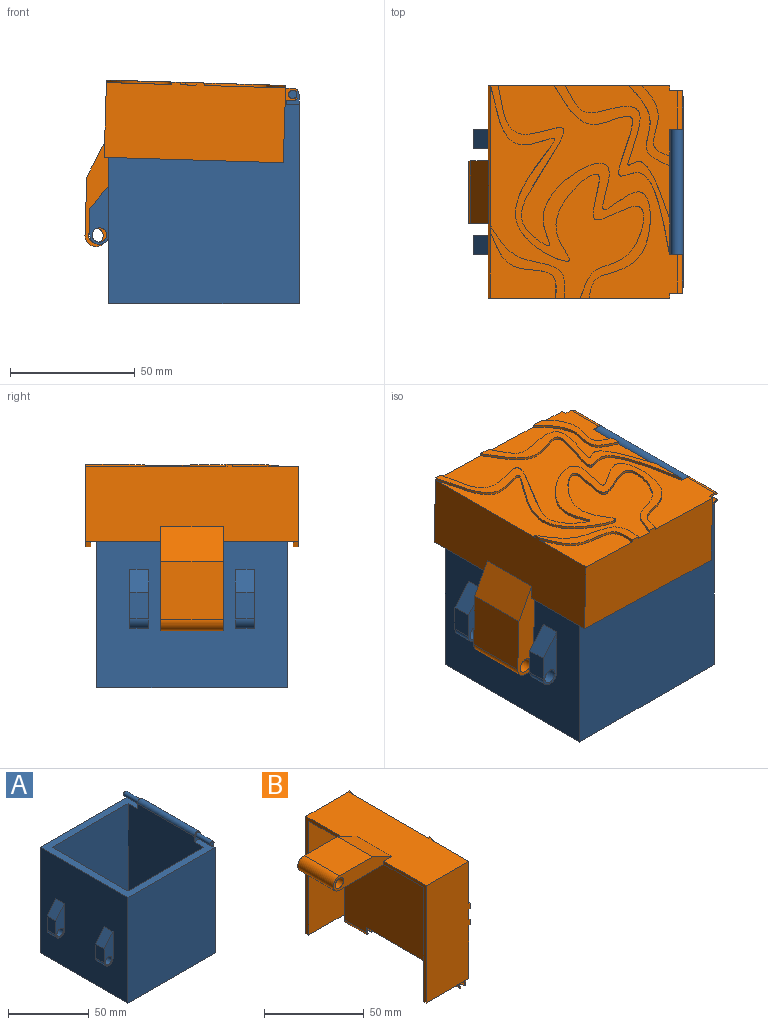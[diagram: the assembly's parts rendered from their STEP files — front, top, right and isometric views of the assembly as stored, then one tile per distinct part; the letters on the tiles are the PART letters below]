
ASSEMBLY  parts=2 mates=1
PART A: 30 faces, bbox 83.9x76.2x86.5 mm
  f0: plane 76.2x76.2mm, normal (0,0,1), area 1174mm2, adj f1,f2,f3,f4,f6,f7,f8,f9
  f1: plane 80x76.2mm, normal (0,-1,0), area 6096mm2, adj f0,f2,f4,f5
  f2: plane 84x76.2mm, normal (1,0,0), area 6296mm2, adj f0,f1,f3,f5,f11,f12,f13
  f3: plane 80x76.2mm, normal (0,1,0), area 6096mm2, adj f0,f2,f4,f5
  f4: plane 80x76.2mm, normal (-1,0,0), area 5796mm2, adj f0,f1,f3,f5,f18,f20,f22,f23
  f5: plane 76.2x76.2mm, normal (0,0,-1), area 5806.4mm2, adj f1,f2,f3,f4
  f6: plane 75x66.2mm, normal (0,1,0), area 4965mm2, adj f0,f7,f9,f10
  f7: plane 79x66.2mm, normal (-1,0,0), area 5165mm2, adj f0,f6,f8,f10,f11,f12,f13
  f8: plane 75x66.2mm, normal (0,-1,0), area 4965mm2, adj f0,f7,f9,f10
  f9: plane 75x66.2mm, normal (1,0,0), area 4965mm2, adj f0,f6,f8,f10
  f10: plane 66.2x66.2mm, normal (0,0,1), area 4382.4mm2, adj f6,f7,f8,f9
  f11: cylinder r=2.5mm len=50mm, axis (0,1,0), area 392.7mm2, adj f2,f7,f12,f13
  f12: plane 6.5x5mm, normal (0,-1,0), area 21.5mm2, adj f0,f2,f7,f11,f16
  f13: plane 6.5x5mm, normal (0,1,0), area 21.5mm2, adj f0,f2,f7,f11,f15
  f14: plane 3.25x3.25mm, normal (0,1,0), area 8.3mm2, adj f15
  f15: cylinder r=1.62mm len=13.1mm, axis (0,1,0), area 133.8mm2, adj f13,f14
  f16: cylinder r=1.62mm len=13.1mm, axis (0,1,0), area 133.8mm2, adj f12,f17
  f17: plane 3.25x3.25mm, normal (0,-1,0), area 8.3mm2, adj f16
  f18: plane 9.22x7.68mm, normal (-0.77,0,0.64), area 90.9mm2, adj f4,f19,f22,f23
  f19: plane 10.58x7.58mm, normal (-1,0,0), area 80.1mm2, adj f18,f20,f22,f23
  f20: cylinder r=3.84mm len=7.68mm, axis (0,1,0), area 91.4mm2, adj f4,f19,f22,f23
  f21: cylinder r=2.89mm len=7.58mm, axis (0,1,0), area 137.5mm2, adj f22,f23
  f22: plane 23.64x7.68mm, normal (0,-1,0), area 113.7mm2, adj f4,f18,f19,f20,f21
  f23: plane 23.64x7.68mm, normal (0,1,0), area 113.7mm2, adj f4,f18,f19,f20,f21
  f24: plane 9.22x7.68mm, normal (-0.77,0,0.64), area 90.9mm2, adj f4,f25,f28,f29
  f25: plane 10.58x7.58mm, normal (-1,0,0), area 80.1mm2, adj f24,f26,f28,f29
  f26: cylinder r=3.84mm len=7.68mm, axis (0,-1,0), area 91.4mm2, adj f4,f25,f28,f29
  f27: cylinder r=2.89mm len=7.58mm, axis (0,-1,0), area 137.5mm2, adj f28,f29
  f28: plane 23.64x7.68mm, normal (0,1,0), area 113.7mm2, adj f4,f24,f25,f26,f27
  f29: plane 23.64x7.68mm, normal (0,-1,0), area 113.7mm2, adj f4,f24,f25,f26,f27
PART B: 49 faces, bbox 66.9x85.3x83.6 mm
  f0: plane 26.87x26.37mm, normal (1,0,0), area 351.9mm2, adj f25,f26,f46
  f1: plane 53.47x42.01mm, normal (1,0,0), area 474.4mm2, adj f22,f24,f41,f43
  f2: plane 85.28x71.97mm, normal (1,0,0), area 2058.4mm2, adj f11,f12,f13,f14,f24,f25,f38,f40
  f3: plane 85.28x65.74mm, normal (1,0,0), area 1684.5mm2, adj f25,f26,f37,f47
  f4: plane 71.85x30.14mm, normal (-1,0,0), area 200mm2, adj f23,f24,f26,f27,f28,f36
  f5: plane 81.28x72.98mm, normal (-1,0,0), area 5775.3mm2, adj f7,f12,f13,f15,f20,f21,f22,f27
  f6: plane 28.27x14.35mm, normal (1,0,0), area 216.2mm2, adj f19,f20,f21,f22,f23,f24,f44
  f7: cylinder r=2.5mm len=15.63mm, axis (0,1,0), area 35.1mm2, adj f5,f8,f12,f13
  f8: plane 15.63x0.61mm, normal (0.82,0,-0.57), area 11.6mm2, adj f7,f9,f12,f13
  f9: cylinder r=1.76mm len=15.63mm, axis (0,1,0), area 139.2mm2, adj f8,f10,f12,f13
  f10: plane 15.63x0.61mm, normal (-0.82,0,-0.57), area 11.6mm2, adj f9,f11,f12,f13
  f11: cylinder r=2.5mm len=15.63mm, axis (0,1,0), area 35.1mm2, adj f2,f10,f12,f13
  f12: plane 5.02x4.99mm, normal (0,-1,0), area 13mm2, adj f2,f5,f7,f8,f9,f10,f11,f14
  f13: plane 5.02x4.99mm, normal (0,1,0), area 13mm2, adj f2,f5,f7,f8,f9,f10,f11,f22
  f14: plane 29.99x2mm, normal (0,0,-1), area 60mm2, adj f2,f12,f25,f29,f30
  f15: cylinder r=2.5mm len=15.63mm, axis (0,-1,0), area 35.1mm2, adj f5,f16,f20,f21
  f16: plane 15.63x0.61mm, normal (0.82,0,-0.57), area 11.6mm2, adj f15,f17,f20,f21
  f17: cylinder r=1.76mm len=15.63mm, axis (0,-1,0), area 139.2mm2, adj f16,f18,f20,f21
  f18: plane 15.63x0.61mm, normal (-0.82,0,-0.57), area 11.6mm2, adj f17,f19,f20,f21
  f19: cylinder r=2.5mm len=15.63mm, axis (0,-1,0), area 35.1mm2, adj f6,f18,f20,f21
  f20: plane 5.02x4.99mm, normal (0,1,0), area 13mm2, adj f5,f6,f15,f16,f17,f18,f19,f23
  f21: plane 5.02x4.99mm, normal (0,-1,0), area 13mm2, adj f5,f6,f15,f16,f17,f18,f19,f22
  f22: plane 50.01x5.99mm, normal (0,0,-1), area 267.5mm2, adj f1,f5,f6,f13,f21,f40,f41,f42
  f23: plane 29.99x2mm, normal (0,0,-1), area 60mm2, adj f4,f6,f20,f24,f27
  f24: plane 71.85x30.99mm, normal (0,1,0), area 2167.4mm2, adj f1,f2,f4,f6,f23,f26,f37,f38
  f25: plane 71.85x30.99mm, normal (0,-1,0), area 2161.9mm2, adj f0,f2,f3,f14,f26,f30,f37,f38
  f26: plane 85.28x30.99mm, normal (0,0,1), area 2416.2mm2, adj f0,f3,f4,f24,f25,f30,f31,f35
  f27: plane 69.85x25mm, normal (0,-1,0), area 1746.2mm2, adj f4,f5,f23,f28
  f28: plane 81.28x56.7mm, normal (0,0,-1), area 2824.4mm2, adj f4,f5,f27,f29,f30,f33,f35,f36
  f29: plane 69.85x25mm, normal (0,1,0), area 1746.2mm2, adj f5,f14,f28,f30
  f30: plane 71.85x30.14mm, normal (-1,0,0), area 200mm2, adj f14,f25,f26,f28,f29,f35
  f31: plane 25x13.87mm, normal (0.44,0,0.9), area 385.4mm2, adj f26,f32,f35,f36
  f32: plane 25x23.4mm, normal (0,0,1), area 584.9mm2, adj f31,f33,f35,f36
  f33: cylinder r=4.37mm len=25mm, axis (0,1,0), area 338.5mm2, adj f28,f32,f35,f36
  f34: cylinder r=2.95mm len=25mm, axis (0,1,0), area 462.6mm2, adj f35,f36
  f35: plane 41.64x8.74mm, normal (0,-1,0), area 270.2mm2, adj f26,f28,f30,f31,f32,f33,f34
  f36: plane 41.64x8.74mm, normal (0,1,0), area 270.2mm2, adj f4,f26,f28,f31,f32,f33,f34
  f37: extruded ~85.28x61.26mm, area 252.6mm2, adj f3,f24,f25,f39
  f38: extruded ~85.28x61.01mm, area 242.9mm2, adj f2,f24,f25,f39
  f39: plane 85.28x67.52mm, normal (1,0,0), area 848mm2, adj f24,f25,f37,f38
  f40: extruded ~67.65x46.31mm, area 106.5mm2, adj f2,f22,f24,f42
  f41: extruded ~53.47x42.01mm, area 90.2mm2, adj f1,f22,f24,f42
  f42: plane 67.65x46.31mm, normal (1,0,0), area 320.5mm2, adj f22,f24,f40,f41
  f43: extruded ~32.04x16.53mm, area 40.2mm2, adj f1,f22,f24,f45
  f44: extruded ~28.27x11.22mm, area 34.2mm2, adj f6,f22,f24,f45
  f45: plane 32.04x16.53mm, normal (1,0,0), area 124.7mm2, adj f22,f24,f43,f44
  f46: extruded ~26.37x26.33mm, area 42.5mm2, adj f0,f25,f26,f48
  f47: extruded ~29.82x29.03mm, area 46.2mm2, adj f3,f25,f26,f48
  f48: plane 30.35x29.03mm, normal (1,0,0), area 143.9mm2, adj f25,f26,f46,f47
PLACE A at identity fixed
PLACE B rot(axis=(0,-1,0),88.3deg) t=(118.48,0.01,45.87)mm
MATE revolute A.f11 <-> B.f7  axis (0,1,0) through (35.6,-25,84)mm
